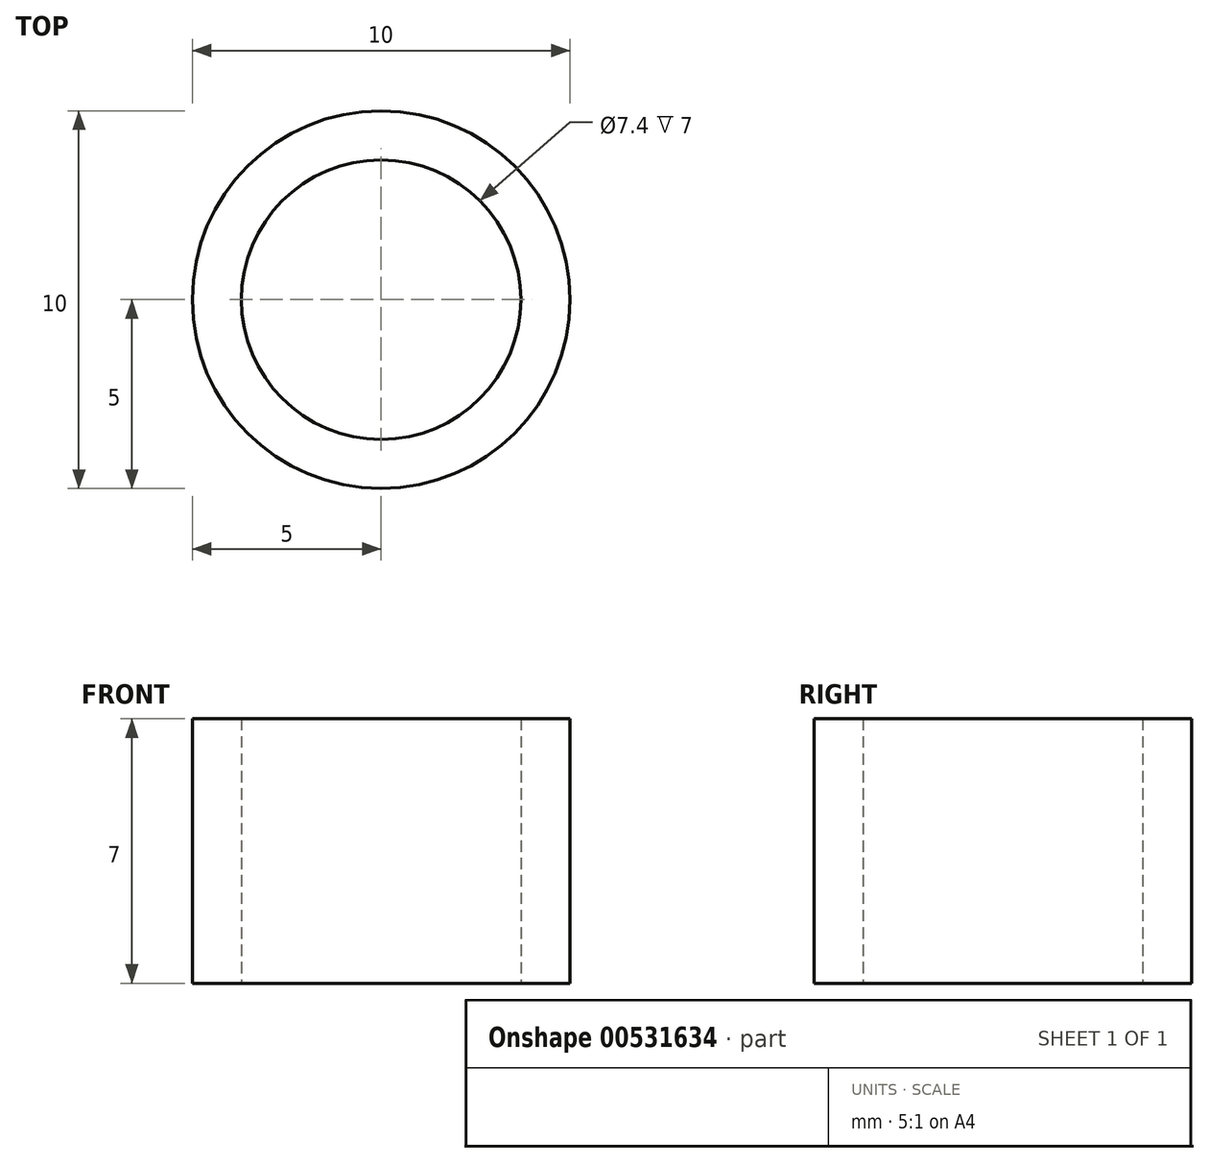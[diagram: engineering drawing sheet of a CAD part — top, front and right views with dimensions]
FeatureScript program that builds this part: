
annotation { "Feature Type Name" : "Feature", "Feature Type Description" : "" }
export const myFeature = defineFeature(function(context is Context, id is Id, definition is map)
    precondition{}
    {
        {
            var Q0;
            Q0=qCreatedBy(makeId("Top.planeOp"),FACE);
            var sketch = newSketch(context, id + "F0", { "sketchPlane" : qUnion([Q0])});
            skCircle(sketch, "E0", {"center": v(0, 0) * mm, "radius": 5 * mm});
            skCircle(sketch, "E1", {"center": v(0, 0) * mm, "radius": 3.7 * mm});
            skSolve(sketch);
        }
        {
            var Q0;
            Q0=makeQuery(id+"F0.imprint","IMPRINT",FACE,{"disambiguationData":[TD([[makeQuery(id+"F0.imprint","IMPRINT",EDGE,{"derivedFrom":sQuery(id+"F0.wireOp",EDGE,"E0")}),1.0]])]});
            extrude(context, id + "F1", {"entities" : qUnion([Q0]), "depth" : 7 * mm, "offsetDistance" : 25 * mm});
        }
    });
